# Revit family: 8fb8c731b6463291471558b7b77a6d66e503b4f8_new
name_source: partatom
category: Furniture
revit_build: Autodesk Revit 2015 (Build: 20140606_1530(x64)
units: mm (PartAtom-declared; Revit-internal decimal feet)

## types (1)
- Parametric
    04 CSI = 12 56 33
    04 CSI Title = Classroom Furniture
    Backrest = Fabric - Mien Company - Mesh - Black
    Base = Plastic - Mien Company - White
    Brochure URL = http://assets1.bywebtrain.com
    Caster = Plastic - Mien Company - Smooth - Black
    Color Availability = Black
    Cut Sheet URL = http://assets1.bywebtrain.com
    Description = Nylon Casters, Black seat, mesh back
    Installation URL = http://assets1.bywebtrain.com
    Manufacturer = MiEN
    Manufacturer Fax = 616-818-1971
    Material = polypropylene
    Model = Nylon Casters, Black seat, mesh back
    Model Number = GYB-3710
    Product Line = Chair
    Product Page URL = http://www.miencompany.com
    Revit Object Download Link = http://library.smartbim.com
    Seat = Fabric - Mien Company - Creased - Black
    Seat Height = 21"
    Seat Height Note = 21In to 25In
    Seat Length = 20"
    Seat Width = 20"
    Subcategory = Task
    Support = Plastic - Mien Company - Smooth - Black
    Surface Finish = polypropylene
    Type Name = Chair
    URL = http://www.miencompany.com
    Weight = 32.00 lb

## geometry (parser evidence)
native form markers: Blend x5, Sweep x9
no freeform markers — native parametric forms only
